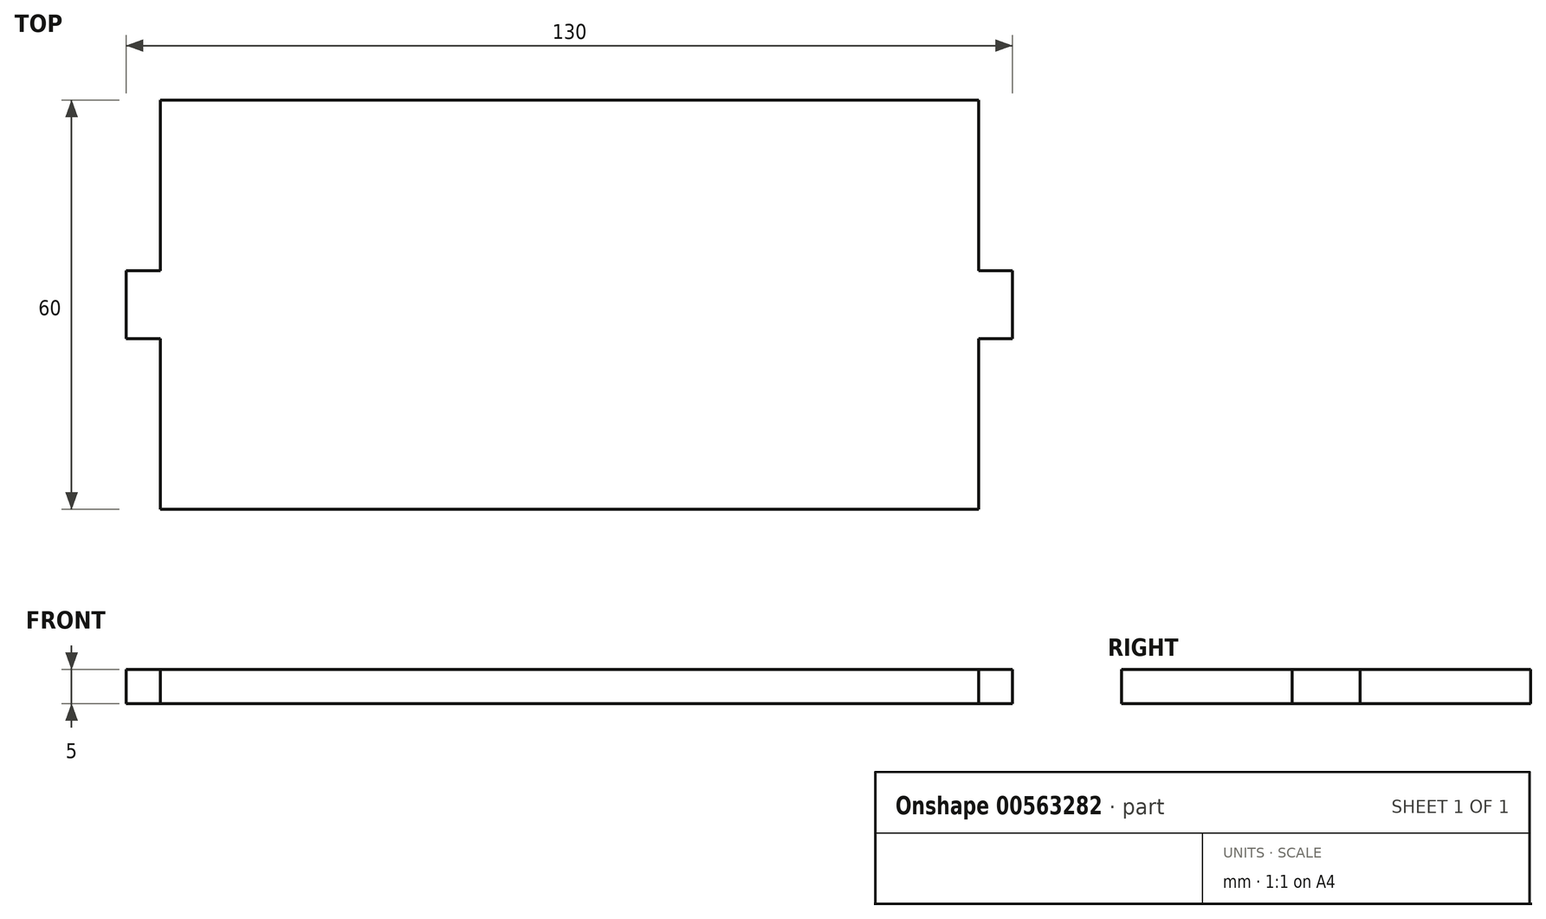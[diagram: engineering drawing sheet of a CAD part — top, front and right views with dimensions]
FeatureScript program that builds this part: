
annotation { "Feature Type Name" : "Feature", "Feature Type Description" : "" }
export const myFeature = defineFeature(function(context is Context, id is Id, definition is map)
    precondition{}
    {
        {
            var Q0;
            Q0=qCreatedBy(makeId("Top.planeOp"),FACE);
            var sketch = newSketch(context, id + "F0", { "sketchPlane" : qUnion([Q0])});
            skLineSegment(sketch, "E0.bottom", {"start": v(-87.63, 35) * mm, "end": v(32.37, 35) * mm});
            skLineSegment(sketch, "E0.top", {"start": v(-87.63, -25) * mm, "end": v(32.37, -25) * mm});
            skLineSegment(sketch, "E0.left", {"start": v(-87.63, 35) * mm, "end": v(-87.63, 10) * mm});
            skLineSegment(sketch, "E0.right", {"start": v(32.37, 35) * mm, "end": v(32.37, 10) * mm});
            skLineSegment(sketch, "E1.bottom", {"start": v(32.37, 10) * mm, "end": v(37.37, 10) * mm});
            skLineSegment(sketch, "E1.top", {"start": v(32.37, 0) * mm, "end": v(37.37, 0) * mm});
            skLineSegment(sketch, "E1.right", {"start": v(37.37, 10) * mm, "end": v(37.37, 0) * mm});
            skLineSegment(sketch, "E2.bottom", {"start": v(-87.63, 10) * mm, "end": v(-92.63, 10) * mm});
            skLineSegment(sketch, "E2.top", {"start": v(-87.63, 0) * mm, "end": v(-92.63, 0) * mm});
            skLineSegment(sketch, "E2.right", {"start": v(-92.63, 10) * mm, "end": v(-92.63, 0) * mm});
            skLineSegment(sketch, "E3.trimOffspring", {"start": v(-87.63, 0) * mm, "end": v(-87.63, -25) * mm});
            skLineSegment(sketch, "E4.trimOffspring", {"start": v(32.37, 0) * mm, "end": v(32.37, -25) * mm});
            skSolve(sketch);
        }
        {
            var Q0;
            Q0=makeQuery(id+"F0.imprint","IMPRINT",FACE,{"disambiguationData":[TD([[makeQuery(id+"F0.imprint","IMPRINT",EDGE,{"derivedFrom":sQuery(id+"F0.wireOp",EDGE,"E0.bottom")}),-1.0]])]});
            extrude(context, id + "F1", {"entities" : qUnion([Q0]), "depth" : 5 * mm, "offsetDistance" : 25 * mm});
        }
    });
